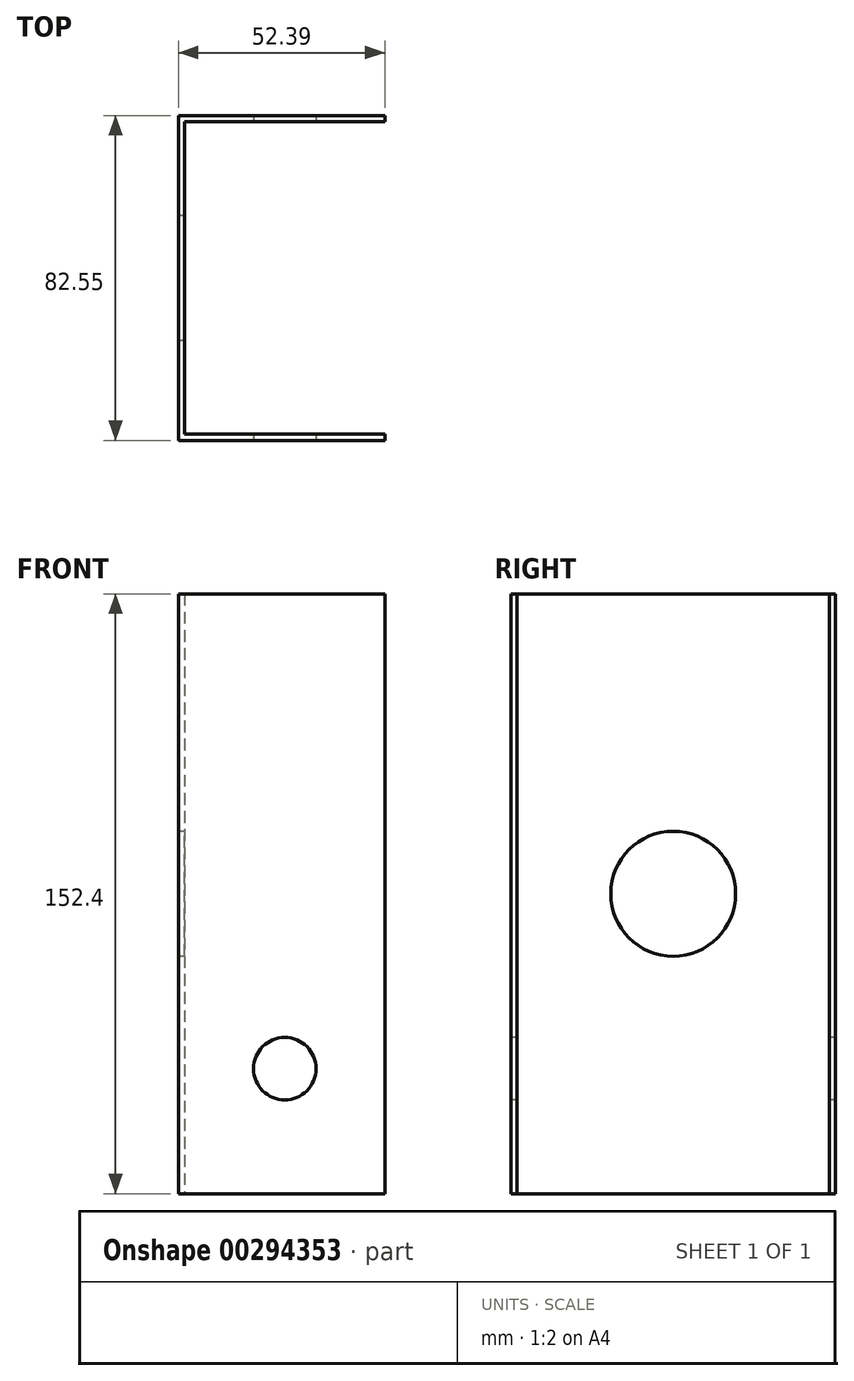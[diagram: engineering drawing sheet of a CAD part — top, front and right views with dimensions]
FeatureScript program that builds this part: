
annotation { "Feature Type Name" : "Feature", "Feature Type Description" : "" }
export const myFeature = defineFeature(function(context is Context, id is Id, definition is map)
    precondition{}
    {
        {
            var Q0;
            Q0=qCreatedBy(makeId("Top.planeOp"),FACE);
            var sketch = newSketch(context, id + "F0", { "sketchPlane" : qUnion([Q0])});
            skLineSegment(sketch, "E0", {"start": v(50.8, 79.38) * mm, "end": v(0, 79.38) * mm});
            skLineSegment(sketch, "E1", {"start": v(0, 79.38) * mm, "end": v(0, 0) * mm});
            skLineSegment(sketch, "E2", {"start": v(0, 0) * mm, "end": v(50.8, 0) * mm});
            skLineSegment(sketch, "E3.0", {"start": v(-1.59, -1.59) * mm, "end": v(50.8, -1.59) * mm});
            skLineSegment(sketch, "E3.1", {"start": v(-1.59, 80.96) * mm, "end": v(-1.59, -1.59) * mm});
            skLineSegment(sketch, "E3.2", {"start": v(50.8, 80.96) * mm, "end": v(-1.59, 80.96) * mm});
            skLineSegment(sketch, "E4", {"start": v(50.8, 80.96) * mm, "end": v(50.8, 79.38) * mm});
            skLineSegment(sketch, "E5", {"start": v(50.8, 0) * mm, "end": v(50.8, -1.59) * mm});
            skSolve(sketch);
        }
        {
            var Q0;
            Q0 = qSketchRegion(id + "F0", true);
            extrude(context, id + "F1", {"entities" : qUnion([Q0]), "depth" : 152.4 * mm});
        }
        {
            var Q0;
            Q0=makeQuery(id+"F1.opExtrude","SWEPT_FACE",FACE,{"disambiguationData":[OSD([sQuery(id+"F0.wireOp",EDGE,"E3.1")])]});
            var sketch = newSketch(context, id + "F2", { "sketchPlane" : qUnion([Q0])});
            skLineSegment(sketch, "E6", {"start": v(-39.69, 152.4) * mm, "end": v(-39.69, 0) * mm, "construction": true});
            skLineSegment(sketch, "E7", {"start": v(-80.96, 76.2) * mm, "end": v(1.59, 76.2) * mm, "construction": true});
            skCircle(sketch, "E8", {"center": v(-39.69, 76.2) * mm, "radius": 15.88 * mm});
            skSolve(sketch);
        }
        {
            var Q0;
            Q0 = qSketchRegion(id + "F2", true);
            extrude(context, id + "F3", {"entities" : qUnion([Q0]), "operationType" : NewBodyOperationType.REMOVE, "oppositeDirection" : true, "depth" : 25.4 * mm});
        }
        {
            var Q0;
            Q0=makeQuery(id+"F1.opExtrude","SWEPT_FACE",FACE,{"disambiguationData":[OSD([sQuery(id+"F0.wireOp",EDGE,"E3.0")])]});
            var sketch = newSketch(context, id + "F4", { "sketchPlane" : qUnion([Q0])});
            skLineSegment(sketch, "E9", {"start": v(25.4, 152.4) * mm, "end": v(25.4, 0) * mm, "construction": true});
            skCircle(sketch, "E10", {"center": v(25.4, 31.75) * mm, "radius": 7.94 * mm});
            skSolve(sketch);
        }
        {
            var Q0;
            Q0 = qSketchRegion(id + "F4", true);
            var Q1;
            Q1=makeQuery(id+"F1.opExtrude","SWEPT_FACE",FACE,{"disambiguationData":[OSD([sQuery(id+"F0.wireOp",EDGE,"E3.2")])]});
            extrude(context, id + "F5", {"entities" : qUnion([Q0]), "operationType" : NewBodyOperationType.REMOVE, "endBound" : BoundingType.UP_TO_SURFACE, "oppositeDirection" : true, "endBoundEntityFace" : qUnion([Q1]), "depth" : 25.4 * mm});
        }
    });
